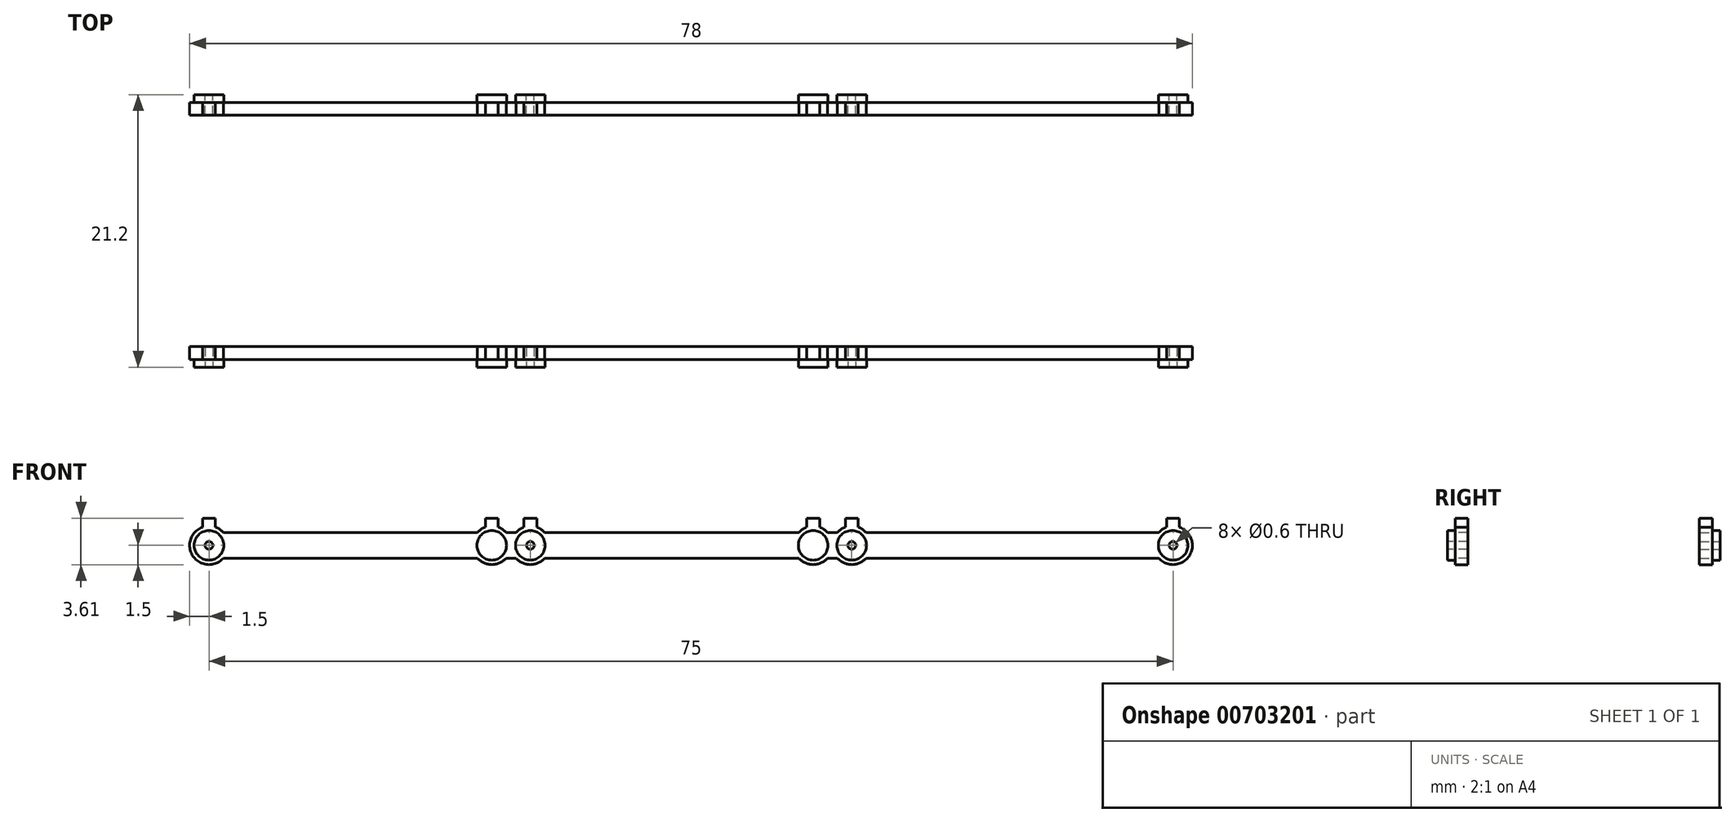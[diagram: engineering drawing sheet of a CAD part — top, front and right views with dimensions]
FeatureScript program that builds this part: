
annotation { "Feature Type Name" : "Feature", "Feature Type Description" : "" }
export const myFeature = defineFeature(function(context is Context, id is Id, definition is map)
    precondition{}
    {
        {
            var Q0;
            Q0=qCreatedBy(makeId("Front.planeOp"),FACE);
            var sketch = newSketch(context, id + "F0", { "sketchPlane" : qUnion([Q0])});
            skLineSegment(sketch, "E0.bottom", {"start": v(-25, 0) * mm, "end": v(50, 0) * mm});
            skLineSegment(sketch, "E0.top", {"start": v(-25, -2) * mm, "end": v(50, -2) * mm});
            skLineSegment(sketch, "E0.left", {"start": v(-25, 0) * mm, "end": v(-25, -2) * mm});
            skLineSegment(sketch, "E0.right", {"start": v(50, 0) * mm, "end": v(50, -2) * mm});
            skCircle(sketch, "E1", {"center": v(-25, -1) * mm, "radius": 1.5 * mm});
            skCircle(sketch, "E2", {"center": v(0, -1) * mm, "radius": 1.5 * mm});
            skCircle(sketch, "E3", {"center": v(25, -1) * mm, "radius": 1.5 * mm});
            skCircle(sketch, "E4", {"center": v(50, -1) * mm, "radius": 1.5 * mm});
            skLineSegment(sketch, "E5.bottom", {"start": v(24.5, 0) * mm, "end": v(25.5, 0) * mm});
            skLineSegment(sketch, "E5.top", {"start": v(24.5, 1.11) * mm, "end": v(25.5, 1.11) * mm});
            skLineSegment(sketch, "E5.left", {"start": v(24.5, 0) * mm, "end": v(24.5, 1.11) * mm});
            skLineSegment(sketch, "E5.right", {"start": v(25.5, 0) * mm, "end": v(25.5, 1.11) * mm});
            skLineSegment(sketch, "E6.bottom", {"start": v(49.5, 0) * mm, "end": v(50.5, 0) * mm});
            skLineSegment(sketch, "E6.top", {"start": v(49.5, 1.11) * mm, "end": v(50.5, 1.11) * mm});
            skLineSegment(sketch, "E6.left", {"start": v(49.5, 0) * mm, "end": v(49.5, 1.11) * mm});
            skLineSegment(sketch, "E6.right", {"start": v(50.5, 0) * mm, "end": v(50.5, 1.11) * mm});
            skLineSegment(sketch, "E7.bottom", {"start": v(-0.5, 0) * mm, "end": v(0.5, 0) * mm});
            skLineSegment(sketch, "E7.top", {"start": v(-0.5, 1.11) * mm, "end": v(0.5, 1.11) * mm});
            skLineSegment(sketch, "E7.left", {"start": v(-0.5, 0) * mm, "end": v(-0.5, 1.11) * mm});
            skLineSegment(sketch, "E7.right", {"start": v(0.5, 0) * mm, "end": v(0.5, 1.11) * mm});
            skLineSegment(sketch, "E8.bottom", {"start": v(-24.5, 0) * mm, "end": v(-25.5, 0) * mm});
            skLineSegment(sketch, "E8.top", {"start": v(-24.5, 1.11) * mm, "end": v(-25.5, 1.11) * mm});
            skLineSegment(sketch, "E8.left", {"start": v(-24.5, 0) * mm, "end": v(-24.5, 1.11) * mm});
            skLineSegment(sketch, "E8.right", {"start": v(-25.5, 0) * mm, "end": v(-25.5, 1.11) * mm});
            skCircle(sketch, "E9", {"center": v(-3, -1) * mm, "radius": 1.5 * mm});
            skLineSegment(sketch, "E10.bottom", {"start": v(-3.5, 0) * mm, "end": v(-2.5, 0) * mm});
            skLineSegment(sketch, "E10.top", {"start": v(-3.5, 1.11) * mm, "end": v(-2.5, 1.11) * mm});
            skLineSegment(sketch, "E10.left", {"start": v(-3.5, 0) * mm, "end": v(-3.5, 1.11) * mm});
            skLineSegment(sketch, "E10.right", {"start": v(-2.5, 0) * mm, "end": v(-2.5, 1.11) * mm});
            skCircle(sketch, "E11", {"center": v(22, -1) * mm, "radius": 1.5 * mm});
            skLineSegment(sketch, "E12.bottom", {"start": v(21.5, 0) * mm, "end": v(22.5, 0) * mm});
            skLineSegment(sketch, "E12.top", {"start": v(21.5, 1.11) * mm, "end": v(22.5, 1.11) * mm});
            skLineSegment(sketch, "E12.left", {"start": v(21.5, 0) * mm, "end": v(21.5, 1.11) * mm});
            skLineSegment(sketch, "E12.right", {"start": v(22.5, 0) * mm, "end": v(22.5, 1.11) * mm});
            skSolve(sketch);
        }
        {
            var Q0;
            Q0 = qSketchRegion(id + "F0", true);
            extrude(context, id + "F1", {"entities" : qUnion([Q0]), "oppositeDirection" : true, "depth" : 1 * mm, "offsetDistance" : 25 * mm});
        }
        {
            var Q0;
            Q0=makeQuery(id+"F1.opExtrude","CAP_FACE",FACE,{"disambiguationData":[OSD([sQuery(id+"F0.wireOp",EDGE,"E0.bottom"),sQuery(id+"F0.wireOp",EDGE,"E0.top"),sQuery(id+"F0.wireOp",EDGE,"E1"),sQuery(id+"F0.wireOp",EDGE,"E2"),sQuery(id+"F0.wireOp",EDGE,"E3"),sQuery(id+"F0.wireOp",EDGE,"E4"),sQuery(id+"F0.wireOp",EDGE,"E5.top"),sQuery(id+"F0.wireOp",EDGE,"E5.left"),sQuery(id+"F0.wireOp",EDGE,"E5.right"),sQuery(id+"F0.wireOp",EDGE,"E6.top"),sQuery(id+"F0.wireOp",EDGE,"E6.left"),sQuery(id+"F0.wireOp",EDGE,"E6.right"),sQuery(id+"F0.wireOp",EDGE,"E7.top"),sQuery(id+"F0.wireOp",EDGE,"E7.left"),sQuery(id+"F0.wireOp",EDGE,"E7.right"),sQuery(id+"F0.wireOp",EDGE,"E8.top"),sQuery(id+"F0.wireOp",EDGE,"E8.left"),sQuery(id+"F0.wireOp",EDGE,"E8.right"),sQuery(id+"F0.wireOp",EDGE,"E9"),sQuery(id+"F0.wireOp",EDGE,"E10.top"),sQuery(id+"F0.wireOp",EDGE,"E10.left"),sQuery(id+"F0.wireOp",EDGE,"E10.right"),sQuery(id+"F0.wireOp",EDGE,"E11"),sQuery(id+"F0.wireOp",EDGE,"E12.top"),sQuery(id+"F0.wireOp",EDGE,"E12.left"),sQuery(id+"F0.wireOp",EDGE,"E12.right")])],"isStart":true});
            var sketch = newSketch(context, id + "F2", { "sketchPlane" : qUnion([Q0])});
            skCircle(sketch, "E13", {"center": v(-25, -1) * mm, "radius": 1.15 * mm});
            skCircle(sketch, "E14", {"center": v(-3, -1) * mm, "radius": 1.15 * mm});
            skCircle(sketch, "E15", {"center": v(0, -1) * mm, "radius": 1.15 * mm});
            skCircle(sketch, "E16", {"center": v(22, -1) * mm, "radius": 1.15 * mm});
            skCircle(sketch, "E17", {"center": v(25, -1) * mm, "radius": 1.15 * mm});
            skCircle(sketch, "E18", {"center": v(50, -1) * mm, "radius": 1.15 * mm});
            skSolve(sketch);
        }
        {
            var Q0;
            Q0 = qSketchRegion(id + "F2", true);
            extrude(context, id + "F3", {"entities" : qUnion([Q0]), "operationType" : NewBodyOperationType.ADD, "depth" : 0.6 * mm, "offsetDistance" : 25 * mm});
        }
        {
            var Q0;
            Q0=makeQuery(id+"F3.opExtrude","CAP_FACE",FACE,{"disambiguationData":[OSD([sQuery(id+"F2.wireOp",EDGE,"E13")])],"isStart":false});
            var sketch = newSketch(context, id + "F4", { "sketchPlane" : qUnion([Q0])});
            skCircle(sketch, "E19", {"center": v(-25, -1) * mm, "radius": 0.3 * mm});
            skSolve(sketch);
        }
        {
            var Q0;
            Q0=makeQuery(id+"F3.opExtrude","CAP_FACE",FACE,{"disambiguationData":[OSD([sQuery(id+"F2.wireOp",EDGE,"E15")])],"isStart":false});
            var sketch = newSketch(context, id + "F5", { "sketchPlane" : qUnion([Q0])});
            skCircle(sketch, "E20", {"center": v(0, -1) * mm, "radius": 0.3 * mm});
            skSolve(sketch);
        }
        {
            var Q0;
            Q0=makeQuery(id+"F3.opExtrude","CAP_FACE",FACE,{"disambiguationData":[OSD([sQuery(id+"F2.wireOp",EDGE,"E17")])],"isStart":false});
            var sketch = newSketch(context, id + "F6", { "sketchPlane" : qUnion([Q0])});
            skCircle(sketch, "E21", {"center": v(25, -1) * mm, "radius": 0.3 * mm});
            skSolve(sketch);
        }
        {
            var Q0;
            Q0=makeQuery(id+"F3.opExtrude","CAP_FACE",FACE,{"disambiguationData":[OSD([sQuery(id+"F2.wireOp",EDGE,"E18")])],"isStart":false});
            var sketch = newSketch(context, id + "F7", { "sketchPlane" : qUnion([Q0])});
            skCircle(sketch, "E22", {"center": v(50, -1) * mm, "radius": 0.3 * mm});
            skSolve(sketch);
        }
        {
            var Q0;
            Q0 = qSketchRegion(id + "F4", true);
            extrude(context, id + "F8", {"entities" : qUnion([Q0]), "operationType" : NewBodyOperationType.REMOVE, "oppositeDirection" : true, "depth" : 2 * mm, "offsetDistance" : 25 * mm});
        }
        {
            var Q0;
            Q0 = qSketchRegion(id + "F5", true);
            extrude(context, id + "F9", {"entities" : qUnion([Q0]), "operationType" : NewBodyOperationType.REMOVE, "oppositeDirection" : true, "depth" : 2 * mm, "offsetDistance" : 25 * mm});
        }
        {
            var Q0;
            Q0 = qSketchRegion(id + "F6", true);
            extrude(context, id + "F10", {"entities" : qUnion([Q0]), "operationType" : NewBodyOperationType.REMOVE, "oppositeDirection" : true, "depth" : 2 * mm, "offsetDistance" : 25 * mm});
        }
        {
            var Q0;
            Q0 = qSketchRegion(id + "F7", true);
            extrude(context, id + "F11", {"entities" : qUnion([Q0]), "operationType" : NewBodyOperationType.REMOVE, "oppositeDirection" : true, "depth" : 2 * mm, "offsetDistance" : 25 * mm});
        }
        {
            var Q0;
            Q0=qCreatedBy(makeId("Front.planeOp"),FACE);
            cPlane(context, id + "F12", {"entities" : qUnion([Q0]), "cplaneType" : CPlaneType.OFFSET, "offset" : 10 * mm, "oppositeDirection" : true, "width" : 150 * mm, "height" : 150 * mm});
        }
        {
            var Q0;
            Q0=makeQuery(id+"F1.opExtrude","SWEPT_BODY",BODY,{"disambiguationData":[OSD([sQuery(id+"F0.wireOp",EDGE,"E0.bottom"),sQuery(id+"F0.wireOp",EDGE,"E0.top"),sQuery(id+"F0.wireOp",EDGE,"E1"),sQuery(id+"F0.wireOp",EDGE,"E2"),sQuery(id+"F0.wireOp",EDGE,"E3"),sQuery(id+"F0.wireOp",EDGE,"E4"),sQuery(id+"F0.wireOp",EDGE,"E5.top"),sQuery(id+"F0.wireOp",EDGE,"E5.left"),sQuery(id+"F0.wireOp",EDGE,"E5.right"),sQuery(id+"F0.wireOp",EDGE,"E6.top"),sQuery(id+"F0.wireOp",EDGE,"E6.left"),sQuery(id+"F0.wireOp",EDGE,"E6.right"),sQuery(id+"F0.wireOp",EDGE,"E7.top"),sQuery(id+"F0.wireOp",EDGE,"E7.left"),sQuery(id+"F0.wireOp",EDGE,"E7.right"),sQuery(id+"F0.wireOp",EDGE,"E8.top"),sQuery(id+"F0.wireOp",EDGE,"E8.left"),sQuery(id+"F0.wireOp",EDGE,"E8.right"),sQuery(id+"F0.wireOp",EDGE,"E9"),sQuery(id+"F0.wireOp",EDGE,"E10.top"),sQuery(id+"F0.wireOp",EDGE,"E10.left"),sQuery(id+"F0.wireOp",EDGE,"E10.right"),sQuery(id+"F0.wireOp",EDGE,"E11"),sQuery(id+"F0.wireOp",EDGE,"E12.top"),sQuery(id+"F0.wireOp",EDGE,"E12.left"),sQuery(id+"F0.wireOp",EDGE,"E12.right")])]});
            var Q1;
            Q1=qCreatedBy(id+"F12.planeOp",FACE);
            mirror(context, id + "F13", {"entities" : qUnion([Q0]), "mirrorPlane" : qUnion([Q1])});
        }
    });
